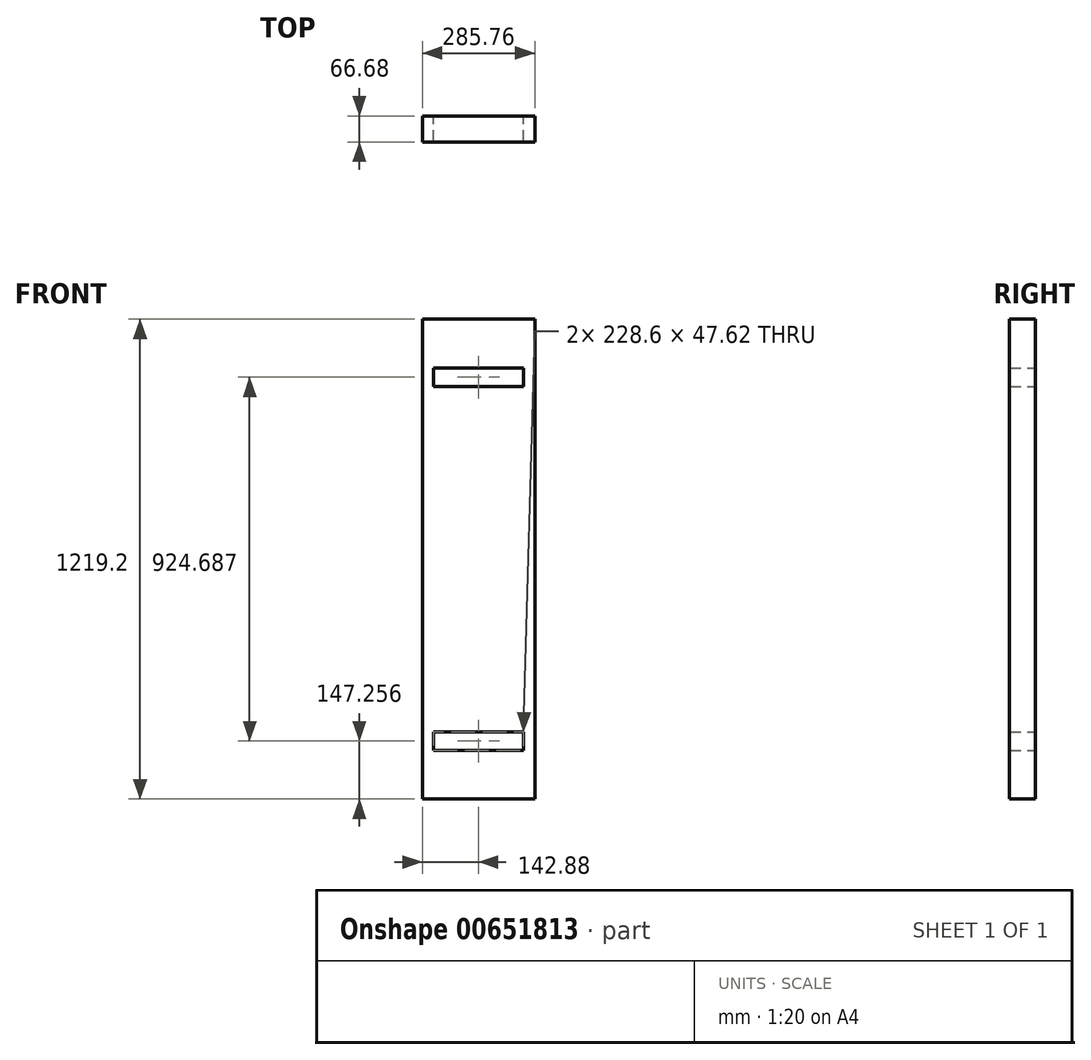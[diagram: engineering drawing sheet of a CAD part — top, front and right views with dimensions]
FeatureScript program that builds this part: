
annotation { "Feature Type Name" : "Feature", "Feature Type Description" : "" }
export const myFeature = defineFeature(function(context is Context, id is Id, definition is map)
    precondition{}
    {
        {
            var Q0;
            Q0=qCreatedBy(makeId("Top.planeOp"),FACE);
            var sketch = newSketch(context, id + "F0", { "sketchPlane" : qUnion([Q0])});
            skLineSegment(sketch, "E0.bottom", {"start": v(142.88, -33.34) * mm, "end": v(-142.88, -33.34) * mm});
            skLineSegment(sketch, "E0.top", {"start": v(142.88, 33.34) * mm, "end": v(-142.88, 33.34) * mm});
            skLineSegment(sketch, "E0.left", {"start": v(142.88, -33.34) * mm, "end": v(142.88, 33.34) * mm});
            skLineSegment(sketch, "E0.right", {"start": v(-142.88, -33.34) * mm, "end": v(-142.88, 33.34) * mm});
            skPoint(sketch, "E0.middle", {"position": v(0, 0) * mm});
            skSolve(sketch);
        }
        {
            var Q0;
            Q0=makeQuery(id+"F0.imprint","IMPRINT",FACE,{"disambiguationData":[TD([[makeQuery(id+"F0.imprint","IMPRINT",EDGE,{"derivedFrom":sQuery(id+"F0.wireOp",EDGE,"E0.bottom")}),-1.0]])]});
            extrude(context, id + "F1", {"entities" : qUnion([Q0]), "depth" : 1219.2 * mm, "offsetDistance" : 25.4 * mm});
        }
        {
            var Q0;
            Q0=makeQuery(id+"F1.opExtrude","SWEPT_FACE",FACE,{"disambiguationData":[OSD([sQuery(id+"F0.wireOp",EDGE,"E0.top")])]});
            var sketch = newSketch(context, id + "F2", { "sketchPlane" : qUnion([Q0])});
            skLineSegment(sketch, "E1", {"start": v(-142.88, 609.6) * mm, "end": v(142.88, 609.6) * mm, "construction": true});
            skLineSegment(sketch, "E2", {"start": v(0, 0) * mm, "end": v(0, 1219.2) * mm, "construction": true});
            skLineSegment(sketch, "E3", {"start": v(-142.88, 1071.94) * mm, "end": v(142.87, 1071.94) * mm, "construction": true});
            skLineSegment(sketch, "E4.MirrorCS", {"start": v(-142.87, 147.26) * mm, "end": v(142.88, 147.26) * mm, "construction": true});
            skLineSegment(sketch, "E5.bottom", {"start": v(114.3, 123.44) * mm, "end": v(-114.3, 123.44) * mm});
            skLineSegment(sketch, "E5.top", {"start": v(114.3, 171.07) * mm, "end": v(-114.3, 171.07) * mm});
            skLineSegment(sketch, "E5.left", {"start": v(114.3, 123.44) * mm, "end": v(114.3, 171.07) * mm});
            skLineSegment(sketch, "E5.right", {"start": v(-114.3, 123.44) * mm, "end": v(-114.3, 171.07) * mm});
            skPoint(sketch, "E5.middle", {"position": v(0, 147.26) * mm});
            skLineSegment(sketch, "E6.MirrorCS", {"start": v(114.3, 1095.76) * mm, "end": v(114.3, 1048.13) * mm});
            skLineSegment(sketch, "E7.MirrorCS", {"start": v(114.3, 1048.13) * mm, "end": v(-114.3, 1048.13) * mm});
            skLineSegment(sketch, "E8.MirrorCS", {"start": v(114.3, 1095.76) * mm, "end": v(-114.3, 1095.76) * mm});
            skPoint(sketch, "E9.MirrorP", {"position": v(0, 1071.94) * mm});
            skLineSegment(sketch, "E10.MirrorCS", {"start": v(-114.3, 1095.76) * mm, "end": v(-114.3, 1048.13) * mm});
            skSolve(sketch);
        }
        {
            var Q0;
            Q0=makeQuery(id+"F2.imprint","IMPRINT",FACE,{"disambiguationData":[TD([[makeQuery(id+"F2.imprint","IMPRINT",EDGE,{"derivedFrom":sQuery(id+"F2.wireOp",EDGE,"E5.bottom")}),-1.0]])]});
            var Q1;
            Q1=makeQuery(id+"F2.imprint","IMPRINT",FACE,{"disambiguationData":[TD([[makeQuery(id+"F2.imprint","IMPRINT",EDGE,{"derivedFrom":sQuery(id+"F2.wireOp",EDGE,"E6.MirrorCS")}),-1.0]])]});
            extrude(context, id + "F3", {"entities" : qUnion([Q0, Q1]), "operationType" : NewBodyOperationType.REMOVE, "endBound" : BoundingType.THROUGH_ALL, "oppositeDirection" : true, "depth" : 25.4 * mm, "offsetDistance" : 25.4 * mm});
        }
    });
